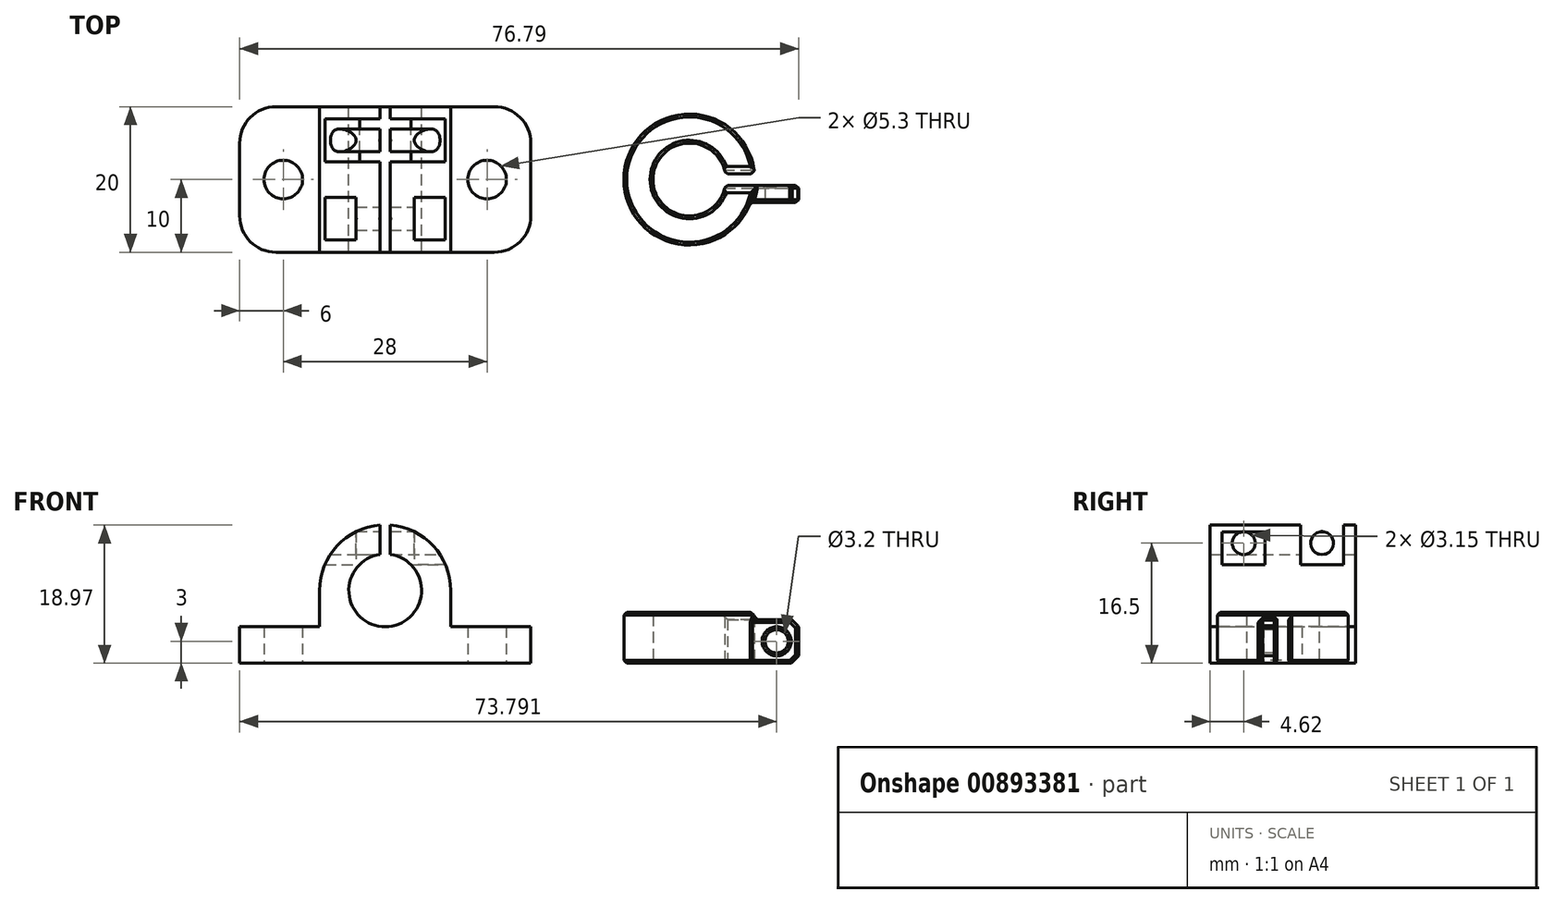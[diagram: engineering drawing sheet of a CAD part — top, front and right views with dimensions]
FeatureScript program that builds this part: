
annotation { "Feature Type Name" : "Feature", "Feature Type Description" : "" }
export const myFeature = defineFeature(function(context is Context, id is Id, definition is map)
    precondition{}
    {
        {
            var Q0;
            Q0=qCreatedBy(makeId("Top.planeOp"),FACE);
            var sketch = newSketch(context, id + "F0", { "sketchPlane" : qUnion([Q0])});
            skLineSegment(sketch, "E0", {"start": v(0, 10) * mm, "end": v(-20, 10) * mm});
            skLineSegment(sketch, "E1", {"start": v(-20, 10) * mm, "end": v(-20, 0) * mm});
            skLineSegment(sketch, "E2.MirrorCS", {"start": v(0, -10) * mm, "end": v(-20, -10) * mm});
            skLineSegment(sketch, "E3.MirrorCS", {"start": v(-20, -10) * mm, "end": v(-20, 0) * mm});
            skLineSegment(sketch, "E4.MirrorCS", {"start": v(0, 10) * mm, "end": v(20, 10) * mm});
            skLineSegment(sketch, "E5.MirrorCS", {"start": v(20, 10) * mm, "end": v(20, 0) * mm});
            skLineSegment(sketch, "E6.MirrorCS", {"start": v(20, -10) * mm, "end": v(20, 0) * mm});
            skLineSegment(sketch, "E7.MirrorCS", {"start": v(0, -10) * mm, "end": v(20, -10) * mm});
            skCircle(sketch, "E8", {"center": v(-14, 0) * mm, "radius": 2.65 * mm});
            skCircle(sketch, "E9.MirrorC", {"center": v(14, 0) * mm, "radius": 2.65 * mm});
            skSolve(sketch);
        }
        {
            var Q0;
            Q0=qCreatedBy(makeId("Front.planeOp"),FACE);
            var sketch = newSketch(context, id + "F1", { "sketchPlane" : qUnion([Q0])});
            skArc(sketch, "E10", {"start": v(-9, 10) * mm, "mid": v(-6.36, 16.36) * mm, "end": v(0, 19) * mm});
            skLineSegment(sketch, "E11", {"start": v(0, 10) * mm, "end": v(-14.1, 10) * mm, "construction": true});
            skLineSegment(sketch, "E12", {"start": v(-9, 10) * mm, "end": v(-9, 0) * mm});
            skCircle(sketch, "E13", {"center": v(0, 10) * mm, "radius": 5 * mm});
            skArc(sketch, "E14.MirrorCS", {"start": v(9, 10) * mm, "mid": v(6.36, 16.36) * mm, "end": v(0, 19) * mm});
            skLineSegment(sketch, "E15.MirrorCS", {"start": v(9, 10) * mm, "end": v(9, 0) * mm});
            skLineSegment(sketch, "E16", {"start": v(-0.7, 18.97) * mm, "end": v(-0.7, 14.95) * mm});
            skLineSegment(sketch, "E17", {"start": v(-9, 0) * mm, "end": v(0, 0) * mm});
            skLineSegment(sketch, "E18.MirrorCS", {"start": v(0.7, 18.97) * mm, "end": v(0.7, 14.95) * mm});
            skLineSegment(sketch, "E19.MirrorCS", {"start": v(9, 0) * mm, "end": v(0, 0) * mm});
            skSolve(sketch);
        }
        {
            var Q0;
            Q0=qCreatedBy(makeId("Right.planeOp"),FACE);
            var sketch = newSketch(context, id + "F2", { "sketchPlane" : qUnion([Q0])});
            skLineSegment(sketch, "E20", {"start": v(-5.38, 21.06) * mm, "end": v(-5.38, -3.64) * mm, "construction": true});
            skCircle(sketch, "E21", {"center": v(-5.38, 16.5) * mm, "radius": 1.57 * mm});
            skLineSegment(sketch, "E22", {"start": v(-8.33, 19.45) * mm, "end": v(-8.33, 13.55) * mm});
            skLineSegment(sketch, "E23", {"start": v(-8.33, 13.55) * mm, "end": v(-5.38, 13.55) * mm});
            skLineSegment(sketch, "E24", {"start": v(-8.33, 19.45) * mm, "end": v(-5.38, 19.45) * mm});
            skLineSegment(sketch, "E25.MirrorCS", {"start": v(-2.43, 19.45) * mm, "end": v(-5.38, 19.45) * mm});
            skLineSegment(sketch, "E26.MirrorCS", {"start": v(-2.43, 19.45) * mm, "end": v(-2.43, 13.55) * mm});
            skLineSegment(sketch, "E27.MirrorCS", {"start": v(-2.43, 13.55) * mm, "end": v(-5.38, 13.55) * mm});
            skLineSegment(sketch, "E28", {"start": v(-11.65, 16.5) * mm, "end": v(-1.1, 16.5) * mm, "construction": true});
            skLineSegment(sketch, "E29.MirrorCS", {"start": v(8.33, 19.45) * mm, "end": v(5.38, 19.45) * mm});
            skLineSegment(sketch, "E30.MirrorCS", {"start": v(8.33, 19.45) * mm, "end": v(8.33, 13.55) * mm});
            skLineSegment(sketch, "E31.MirrorCS", {"start": v(8.33, 13.55) * mm, "end": v(5.38, 13.55) * mm});
            skLineSegment(sketch, "E32.MirrorCS", {"start": v(2.43, 13.55) * mm, "end": v(5.38, 13.55) * mm});
            skLineSegment(sketch, "E33.MirrorCS", {"start": v(2.43, 19.45) * mm, "end": v(2.43, 13.55) * mm});
            skLineSegment(sketch, "E34.MirrorCS", {"start": v(2.43, 19.45) * mm, "end": v(5.38, 19.45) * mm});
            skCircle(sketch, "E35.MirrorC", {"center": v(5.38, 16.5) * mm, "radius": 1.57 * mm});
            skSolve(sketch);
        }
        {
            var Q0;
            Q0=makeQuery(id+"F0.imprint","IMPRINT",FACE,{"disambiguationData":[TD([[makeQuery(id+"F0.imprint","IMPRINT",EDGE,{"derivedFrom":sQuery(id+"F0.wireOp",EDGE,"E0")}),1.0]])]});
            extrude(context, id + "F3", {"entities" : qUnion([Q0]), "depth" : 5 * mm, "offsetDistance" : 25 * mm});
        }
        {
            var Q0;
            {var subQ3=sQuery(id+"F1.wireOp",EDGE,"E12");Q0=makeQuery(id+"F1.imprint","IMPRINT",FACE,{"disambiguationData":[TD([[makeQuery(id+"F1.imprint","IMPRINT",EDGE,{"derivedFrom":subQ3}),1.0]])]});}
            extrude(context, id + "F4", {"entities" : qUnion([Q0]), "operationType" : NewBodyOperationType.ADD, "endBound" : BoundingType.SYMMETRIC, "depth" : 20 * mm, "offsetDistance" : 25 * mm});
        }
        {
            var Q0;
            Q0=makeQuery(id+"F2.imprint","IMPRINT",FACE,{"disambiguationData":[TD([[makeQuery(id+"F2.imprint","IMPRINT",EDGE,{"derivedFrom":sQuery(id+"F2.wireOp",EDGE,"E21")}),1.0]])]});
            var Q1;
            Q1=makeQuery(id+"F2.imprint","IMPRINT",FACE,{"disambiguationData":[TD([[makeQuery(id+"F2.imprint","IMPRINT",EDGE,{"derivedFrom":sQuery(id+"F2.wireOp",EDGE,"E35.MirrorC")}),-1.0]])]});
            extrude(context, id + "F5", {"entities" : qUnion([Q0, Q1]), "operationType" : NewBodyOperationType.REMOVE, "endBound" : BoundingType.SYMMETRIC, "oppositeDirection" : true, "depth" : 25 * mm, "offsetDistance" : 25 * mm});
        }
        {
            var Q0;
            Q0=makeQuery(id+"F2.imprint","IMPRINT",FACE,{"disambiguationData":[TD([[makeQuery(id+"F2.imprint","IMPRINT",EDGE,{"derivedFrom":sQuery(id+"F2.wireOp",EDGE,"E21")}),-1.0]])]});
            var Q1;
            Q1=makeQuery(id+"F2.imprint","IMPRINT",FACE,{"disambiguationData":[TD([[makeQuery(id+"F2.imprint","IMPRINT",EDGE,{"derivedFrom":sQuery(id+"F2.wireOp",EDGE,"E29.MirrorCS")}),1.0]])]});
            extrude(context, id + "F6", {"entities" : qUnion([Q0, Q1]), "operationType" : NewBodyOperationType.REMOVE, "oppositeDirection" : true, "depth" : 25 * mm, "offsetDistance" : 25 * mm, "hasSecondDirection" : true, "secondDirectionOppositeDirection" : true, "secondDirectionDepth" : 4 * mm});
        }
        {
            var Q0;
            Q0=makeQuery(id+"F2.imprint","IMPRINT",FACE,{"disambiguationData":[TD([[makeQuery(id+"F2.imprint","IMPRINT",EDGE,{"derivedFrom":sQuery(id+"F2.wireOp",EDGE,"E21")}),-1.0]])]});
            var Q1;
            Q1=makeQuery(id+"F2.imprint","IMPRINT",FACE,{"disambiguationData":[TD([[makeQuery(id+"F2.imprint","IMPRINT",EDGE,{"derivedFrom":sQuery(id+"F2.wireOp",EDGE,"E29.MirrorCS")}),1.0]])]});
            extrude(context, id + "F7", {"entities" : qUnion([Q0, Q1]), "operationType" : NewBodyOperationType.REMOVE, "depth" : 25 * mm, "offsetDistance" : 25 * mm, "hasSecondDirection" : true, "secondDirectionOppositeDirection" : false, "secondDirectionDepth" : 4 * mm});
        }
        {
            var Q0;
            Q0=makeQuery(id+"F3.opExtrude","SWEPT_EDGE",EDGE,{"disambiguationData":[OSD([sQuery(id+"F0.wireOp",EDGE,"E2.MirrorCS"),sQuery(id+"F0.wireOp",EDGE,"E3.MirrorCS")])]});
            var Q1;
            Q1=makeQuery(id+"F3.opExtrude","SWEPT_EDGE",EDGE,{"disambiguationData":[OSD([sQuery(id+"F0.wireOp",EDGE,"E0"),sQuery(id+"F0.wireOp",EDGE,"E1")])]});
            var Q2;
            Q2=makeQuery(id+"F3.opExtrude","SWEPT_EDGE",EDGE,{"disambiguationData":[OSD([sQuery(id+"F0.wireOp",EDGE,"E6.MirrorCS"),sQuery(id+"F0.wireOp",EDGE,"E7.MirrorCS")])]});
            var Q3;
            Q3=makeQuery(id+"F3.opExtrude","SWEPT_EDGE",EDGE,{"disambiguationData":[OSD([sQuery(id+"F0.wireOp",EDGE,"E4.MirrorCS"),sQuery(id+"F0.wireOp",EDGE,"E5.MirrorCS")])]});
            fillet(context, id + "F8", {"entities" : qUnion([Q0, Q1, Q2, Q3]), "radius" : 5 * mm, "tangentPropagation" : true, "allowEdgeOverflow" : false});
        }
        {
            var Q0;
            Q0=qCreatedBy(makeId("Top.planeOp"),FACE);
            var sketch = newSketch(context, id + "F9", { "sketchPlane" : qUnion([Q0])});
            skCircle(sketch, "E36", {"center": v(41.8, 0) * mm, "radius": 5 * mm});
            skCircle(sketch, "E37", {"center": v(41.8, 0) * mm, "radius": 9 * mm});
            skLineSegment(sketch, "E38", {"start": v(46.73, 0.8) * mm, "end": v(56.8, 0.8) * mm});
            skLineSegment(sketch, "E39", {"start": v(56.8, 3.16) * mm, "end": v(50.22, 3.16) * mm});
            skLineSegment(sketch, "E40", {"start": v(50.22, 3.16) * mm, "end": v(56.8, 3.16) * mm});
            skLineSegment(sketch, "E41", {"start": v(56.8, 0.8) * mm, "end": v(56.8, 3.16) * mm});
            skLineSegment(sketch, "E42.MirrorCS", {"start": v(46.73, -0.8) * mm, "end": v(56.8, -0.8) * mm});
            skLineSegment(sketch, "E43.MirrorCS", {"start": v(56.8, -3.16) * mm, "end": v(50.22, -3.16) * mm});
            skLineSegment(sketch, "E44.MirrorCS", {"start": v(56.8, -0.8) * mm, "end": v(56.8, -3.16) * mm});
            skSolve(sketch);
        }
        {
            var Q0;
            Q0=qCreatedBy(makeId("Front.planeOp"),FACE);
            var sketch = newSketch(context, id + "F10", { "sketchPlane" : qUnion([Q0])});
            skCircle(sketch, "E45", {"center": v(53.8, 3) * mm, "radius": 1.6 * mm});
            skSolve(sketch);
        }
        {
            var Q0;
            {var subQ5=sQuery(id+"F9.wireOp",EDGE,"E38");var subQ7=sQuery(id+"F9.wireOp",EDGE,"E36");var subQ8=makeQuery(id+"F9.imprint","INTERSECT",VERTEX,{"derivedFrom":[subQ7,subQ5]});Q0=makeQuery(id+"F9.imprint","IMPRINT",FACE,{"disambiguationData":[TD([[makeQuery(id+"F9.imprint","IMPRINT",EDGE,{"disambiguationData":[TD([[subQ8,-1.0]])],"derivedFrom":subQ7}),-1.0]])]});}
            var Q1;
            {var subQ0=sQuery(id+"F9.wireOp",EDGE,"E40");Q1=makeQuery(id+"F9.imprint","IMPRINT",FACE,{"disambiguationData":[TD([[makeQuery(id+"F9.imprint","IMPRINT",EDGE,{"derivedFrom":subQ0}),-1.0]])]});}
            var Q2;
            {var subQ0=sQuery(id+"F9.wireOp",EDGE,"E43.MirrorCS");Q2=makeQuery(id+"F9.imprint","IMPRINT",FACE,{"disambiguationData":[TD([[makeQuery(id+"F9.imprint","IMPRINT",EDGE,{"derivedFrom":subQ0}),-1.0]])]});}
            extrude(context, id + "F11", {"entities" : qUnion([Q0, Q1, Q2]), "depth" : 6 * mm, "offsetDistance" : 25 * mm});
        }
        {
            var Q0;
            {var subQ5=sQuery(id+"F9.wireOp",EDGE,"E38");var subQ7=sQuery(id+"F9.wireOp",EDGE,"E36");var subQ8=makeQuery(id+"F9.imprint","INTERSECT",VERTEX,{"derivedFrom":[subQ7,subQ5]});Q0=makeQuery(id+"F9.imprint","IMPRINT",FACE,{"disambiguationData":[TD([[makeQuery(id+"F9.imprint","IMPRINT",EDGE,{"disambiguationData":[TD([[subQ8,-1.0]])],"derivedFrom":subQ7}),-1.0]])]});}
            extrude(context, id + "F12", {"entities" : qUnion([Q0]), "operationType" : NewBodyOperationType.ADD, "depth" : 7 * mm, "offsetDistance" : 25 * mm});
        }
        {
            var Q0;
            Q0=makeQuery(id+"F10.imprint","IMPRINT",FACE,{"disambiguationData":[TD([[makeQuery(id+"F10.imprint","IMPRINT",EDGE,{"derivedFrom":sQuery(id+"F10.wireOp",EDGE,"E45")}),1.0]])]});
            extrude(context, id + "F13", {"entities" : qUnion([Q0]), "operationType" : NewBodyOperationType.REMOVE, "endBound" : BoundingType.SYMMETRIC, "oppositeDirection" : true, "depth" : 25 * mm, "offsetDistance" : 25 * mm});
        }
        {
            var Q0;
            Q0=makeQuery(id+"F11.opExtrude","CAP_EDGE",EDGE,{"disambiguationData":[OSD([sQuery(id+"F9.wireOp",EDGE,"E41")])],"isStart":false});
            var Q1;
            Q1=makeQuery(id+"F11.opExtrude","CAP_EDGE",EDGE,{"disambiguationData":[OSD([sQuery(id+"F9.wireOp",EDGE,"E44.MirrorCS")])],"isStart":false});
            var Q2;
            Q2=makeQuery(id+"F11.opExtrude","CAP_EDGE",EDGE,{"disambiguationData":[OSD([sQuery(id+"F9.wireOp",EDGE,"E44.MirrorCS")])],"isStart":true});
            var Q3;
            Q3=makeQuery(id+"F11.opExtrude","CAP_EDGE",EDGE,{"disambiguationData":[OSD([sQuery(id+"F9.wireOp",EDGE,"E41")])],"isStart":true});
            var Q4;
            Q4=makeQuery(id+"F12.opExtrude","CAP_EDGE",EDGE,{"disambiguationData":[OSD([sQuery(id+"F9.wireOp",EDGE,"E38")])],"isStart":false});
            var Q5;
            Q5=makeQuery(id+"F12.opExtrude","CAP_EDGE",EDGE,{"disambiguationData":[OSD([sQuery(id+"F9.wireOp",EDGE,"E42.MirrorCS")])],"isStart":false});
            chamfer(context, id + "F14", {"entities" : qUnion([Q0, Q1, Q2, Q3, Q4, Q5]), "width" : 1 * mm, "tangentPropagation" : true});
        }
        {
            var Q0;
            Q0=makeQuery(id+"F12.opExtrude","CAP_EDGE",EDGE,{"disambiguationData":[OSD([sQuery(id+"F9.wireOp",EDGE,"E36")])],"isStart":false});
            var Q1;
            Q1=makeQuery(id+"F12.opExtrude","CAP_EDGE",EDGE,{"disambiguationData":[OSD([sQuery(id+"F9.wireOp",EDGE,"E37")])],"isStart":false});
            var Q2;
            Q2=makeQuery(id+"F11.opExtrude","SWEPT_EDGE",EDGE,{"disambiguationData":[OSD([sQuery(id+"F9.wireOp",EDGE,"E38"),sQuery(id+"F9.wireOp",EDGE,"E41")])]});
            var Q3;
            Q3=makeQuery(id+"F11.opExtrude","SWEPT_EDGE",EDGE,{"disambiguationData":[OSD([sQuery(id+"F9.wireOp",EDGE,"E42.MirrorCS"),sQuery(id+"F9.wireOp",EDGE,"E44.MirrorCS")])]});
            var Q4;
            Q4=makeQuery(id+"F11.opExtrude","SWEPT_EDGE",EDGE,{"disambiguationData":[OSD([sQuery(id+"F9.wireOp",EDGE,"E43.MirrorCS"),sQuery(id+"F9.wireOp",EDGE,"E44.MirrorCS")])]});
            var Q5;
            Q5=makeQuery(id+"F11.opExtrude","SWEPT_FACE",FACE,{"disambiguationData":[OSD([sQuery(id+"F9.wireOp",EDGE,"E43.MirrorCS")])]});
            var Q6;
            Q6=makeQuery(id+"F11.opExtrude","SWEPT_FACE",FACE,{"disambiguationData":[OSD([sQuery(id+"F9.wireOp",EDGE,"E40")])]});
            var Q7;
            {var subQ0=sQuery(id+"F9.wireOp",EDGE,"E38");var subQ1=sQuery(id+"F9.wireOp",EDGE,"E36");Q7=makeQuery(id+"F12.boolean.opBoolean","MERGE",EDGE,{"derivedFrom":[makeQuery(id+"F11.opExtrude","SWEPT_EDGE",EDGE,{"disambiguationData":[OSD([subQ1,subQ0])]}),makeQuery(id+"F12.opExtrude","SWEPT_EDGE",EDGE,{"disambiguationData":[OSD([subQ1,subQ0])]})]});}
            var Q8;
            {var subQ0=sQuery(id+"F9.wireOp",EDGE,"E42.MirrorCS");var subQ1=sQuery(id+"F9.wireOp",EDGE,"E36");Q8=makeQuery(id+"F12.boolean.opBoolean","MERGE",EDGE,{"derivedFrom":[makeQuery(id+"F11.opExtrude","SWEPT_EDGE",EDGE,{"disambiguationData":[OSD([subQ1,subQ0])]}),makeQuery(id+"F12.opExtrude","SWEPT_EDGE",EDGE,{"disambiguationData":[OSD([subQ1,subQ0])]})]});}
            var Q9;
            Q9=makeQuery(id+"F11.opExtrude","CAP_EDGE",EDGE,{"disambiguationData":[OSD([sQuery(id+"F9.wireOp",EDGE,"E42.MirrorCS")])],"isStart":true});
            var Q10;
            Q10=makeQuery(id+"F11.opExtrude","CAP_EDGE",EDGE,{"disambiguationData":[OSD([sQuery(id+"F9.wireOp",EDGE,"E38")])],"isStart":true});
            var Q11;
            {var subQ0=sQuery(id+"F9.wireOp",EDGE,"E42.MirrorCS");Q11=makeQuery(id+"F13.boolean.opBoolean","INTERSECT",EDGE,{"derivedFrom":[makeQuery(id+"F12.boolean.opBoolean","MERGE",FACE,{"derivedFrom":[makeQuery(id+"F11.opExtrude","SWEPT_FACE",FACE,{"disambiguationData":[OSD([subQ0])]}),makeQuery(id+"F12.opExtrude","SWEPT_FACE",FACE,{"disambiguationData":[OSD([subQ0])]})]}),makeQuery(id+"F13.opExtrude","SWEPT_FACE",FACE,{"disambiguationData":[OSD([sQuery(id+"F10.wireOp",EDGE,"E45")])]})]});}
            var Q12;
            {var subQ0=sQuery(id+"F9.wireOp",EDGE,"E38");Q12=makeQuery(id+"F13.boolean.opBoolean","INTERSECT",EDGE,{"derivedFrom":[makeQuery(id+"F12.boolean.opBoolean","MERGE",FACE,{"derivedFrom":[makeQuery(id+"F11.opExtrude","SWEPT_FACE",FACE,{"disambiguationData":[OSD([subQ0])]}),makeQuery(id+"F12.opExtrude","SWEPT_FACE",FACE,{"disambiguationData":[OSD([subQ0])]})]}),makeQuery(id+"F13.opExtrude","SWEPT_FACE",FACE,{"disambiguationData":[OSD([sQuery(id+"F10.wireOp",EDGE,"E45")])]})]});}
            var Q13;
            {var subQ0=sQuery(id+"F9.wireOp",EDGE,"E38");Q13=makeQuery(id+"F14.opChamfer","BLEND_EDGE",EDGE,{"blendedFrom":[makeQuery(id+"F11.opExtrude","CAP_EDGE",EDGE,{"disambiguationData":[OSD([sQuery(id+"F9.wireOp",EDGE,"E41")])],"isStart":true}),makeQuery(id+"F12.boolean.opBoolean","MERGE",FACE,{"derivedFrom":[makeQuery(id+"F11.opExtrude","SWEPT_FACE",FACE,{"disambiguationData":[OSD([subQ0])]}),makeQuery(id+"F12.opExtrude","SWEPT_FACE",FACE,{"disambiguationData":[OSD([subQ0])]})]})],"blendedInto":[makeQuery(id+"F12.boolean.opBoolean","MERGE",FACE,{"derivedFrom":[makeQuery(id+"F11.opExtrude","SWEPT_FACE",FACE,{"disambiguationData":[OSD([subQ0])]}),makeQuery(id+"F12.opExtrude","SWEPT_FACE",FACE,{"disambiguationData":[OSD([subQ0])]})]})]});}
            var Q14;
            {var subQ0=sQuery(id+"F9.wireOp",EDGE,"E42.MirrorCS");Q14=makeQuery(id+"F14.opChamfer","BLEND_EDGE",EDGE,{"blendedFrom":[makeQuery(id+"F11.opExtrude","CAP_EDGE",EDGE,{"disambiguationData":[OSD([sQuery(id+"F9.wireOp",EDGE,"E44.MirrorCS")])],"isStart":true}),makeQuery(id+"F12.boolean.opBoolean","MERGE",FACE,{"derivedFrom":[makeQuery(id+"F11.opExtrude","SWEPT_FACE",FACE,{"disambiguationData":[OSD([subQ0])]}),makeQuery(id+"F12.opExtrude","SWEPT_FACE",FACE,{"disambiguationData":[OSD([subQ0])]})]})],"blendedInto":[makeQuery(id+"F12.boolean.opBoolean","MERGE",FACE,{"derivedFrom":[makeQuery(id+"F11.opExtrude","SWEPT_FACE",FACE,{"disambiguationData":[OSD([subQ0])]}),makeQuery(id+"F12.opExtrude","SWEPT_FACE",FACE,{"disambiguationData":[OSD([subQ0])]})]})]});}
            var Q15;
            {var subQ0=sQuery(id+"F9.wireOp",EDGE,"E41");Q15=makeQuery(id+"F14.opChamfer","BLEND_FACE",FACE,{"disambiguationData":[OSD([subQ0]),TDD([makeQuery(id+"F11.opExtrude","CAP_EDGE",EDGE,{"disambiguationData":[OSD([subQ0])],"isStart":false})])]});}
            var Q16;
            {var subQ0=sQuery(id+"F9.wireOp",EDGE,"E44.MirrorCS");Q16=makeQuery(id+"F14.opChamfer","BLEND_FACE",FACE,{"disambiguationData":[OSD([subQ0]),TDD([makeQuery(id+"F11.opExtrude","CAP_EDGE",EDGE,{"disambiguationData":[OSD([subQ0])],"isStart":false})])]});}
            chamfer(context, id + "F15", {"entities" : qUnion([Q0, Q1, Q2, Q3, Q4, Q5, Q6, Q7, Q8, Q9, Q10, Q11, Q12, Q13, Q14, Q15, Q16]), "width" : 0.4 * mm, "tangentPropagation" : true});
        }
    });
